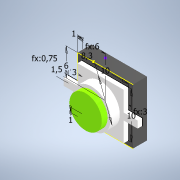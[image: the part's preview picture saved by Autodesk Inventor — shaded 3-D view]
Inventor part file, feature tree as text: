
AUTODESK INVENTOR PART (.ipt)
format: ipt  version: 2022.2 (Build 262287000, 287)  size: 162,304 bytes
history: native  units: mm
features: extrude x4, sketch x3, imported_body x1
ambient origin geometry x8: Origin, YZ Plane, XZ Plane, XY Plane, X Axis, Y Axis, Z Axis, Center Point
bodies: Solid1 (feature_tree)
feature tree (8):
  extrude  "Extrusion1"  Depth=10.0mm
  sketch  "Sketch2"  dims[d3=10.0mm d4=1.0mm]
  extrude  "Extrusion2"  Depth=1.0mm
  extrude  "Extrusion3"  Depth=6.0mm
  extrude  "Extrusion4"  Depth=6.0mm
  sketch  "Sketch1"  dims[d0=4.5mm d1=0.0mm d2=10.0mm]
  sketch  "Sketch3"  dims[d5=1.0mm d6=6.0mm d7=6.0mm d8=8.3mm d9=1.0mm d10=0.0mm d11=3.0mm d12=0.0mm d13=7.0mm d14=1.25mm d15=0.0mm d20=3.0mm d21=3.0mm d22=1.5mm d23=0.75mm]
  imported_body  "Base1"
